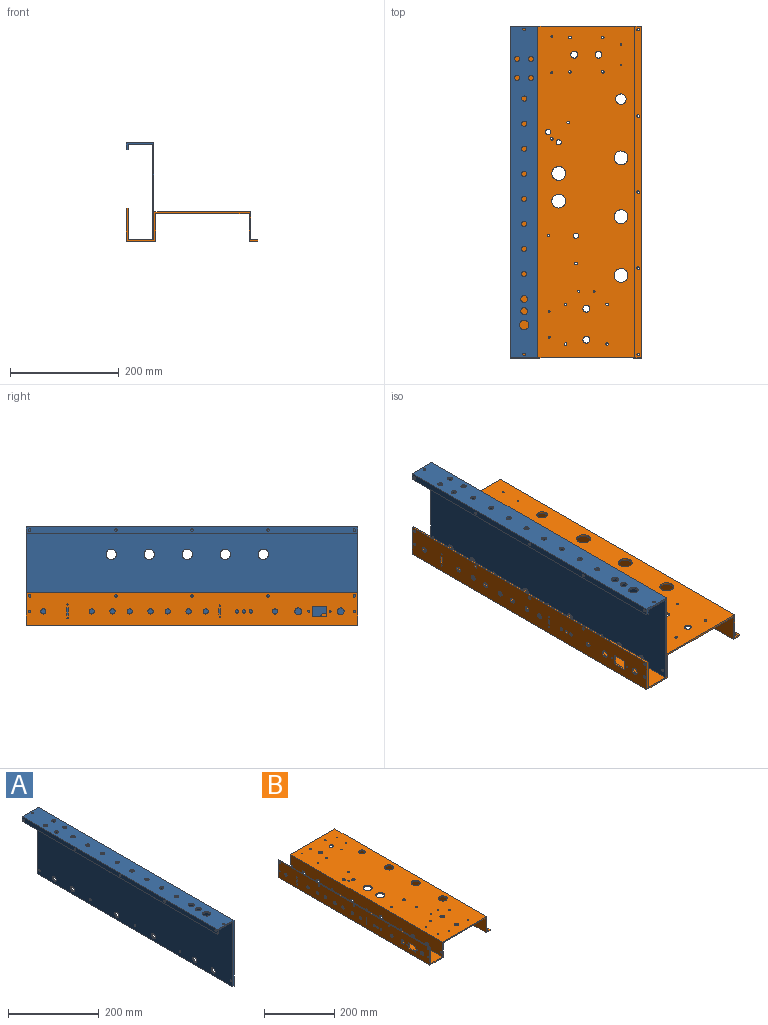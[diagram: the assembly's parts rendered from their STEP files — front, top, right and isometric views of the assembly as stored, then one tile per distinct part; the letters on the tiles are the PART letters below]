
ASSEMBLY  parts=2 mates=1
PART A: 48 faces, bbox 50.8x609.6x177.8 mm
  f0: plane 609.6x50.8mm, normal (0,0,1), area 29584.1mm2, adj f1,f7,f8,f9,f31,f32,f33,f34
  f1: plane 609.6x12.7mm, normal (-1,0,0), area 7652.9mm2, adj f0,f2,f8,f9,f26,f27,f28,f29
  f2: plane 609.6x3.18mm, normal (0,0,-1), area 1935.5mm2, adj f1,f3,f8,f9
  f3: plane 609.6x9.53mm, normal (1,0,0), area 5717.4mm2, adj f2,f4,f8,f9,f26,f27,f28,f29
  f4: plane 609.6x44.45mm, normal (0,0,-1), area 25713.2mm2, adj f3,f5,f8,f9,f31,f32,f33,f34
  f5: plane 609.6x174.63mm, normal (-1,0,0), area 104177.2mm2, adj f4,f6,f8,f9,f10,f11,f12,f13
  f6: plane 609.6x3.18mm, normal (0,0,-1), area 1935.5mm2, adj f5,f7,f8,f9
  f7: plane 609.6x177.8mm, normal (1,0,0), area 106112.6mm2, adj f0,f6,f8,f9,f10,f11,f12,f13
  f8: plane 177.8x50.8mm, normal (0,-1,0), area 746mm2, adj f0,f1,f2,f3,f4,f5,f6,f7
  f9: plane 177.8x50.8mm, normal (0,1,0), area 746mm2, adj f0,f1,f2,f3,f4,f5,f6,f7
  f10: cylinder r=9.53mm len=19.05mm, axis (1,0,0), area 190mm2, adj f5,f7
  f11: cylinder r=2.38mm len=4.76mm, axis (1,0,0), area 47.5mm2, adj f5,f7
  f12: cylinder r=6.35mm len=12.7mm, axis (1,0,0), area 126.7mm2, adj f5,f7
  f13: cylinder r=6.35mm len=12.7mm, axis (1,0,0), area 126.7mm2, adj f5,f7
  f14: cylinder r=2.38mm len=4.76mm, axis (1,0,0), area 47.5mm2, adj f5,f7
  f15: cylinder r=6.35mm len=12.7mm, axis (1,0,0), area 126.7mm2, adj f5,f7
  f16: cylinder r=2.38mm len=4.76mm, axis (1,0,0), area 47.5mm2, adj f5,f7
  f17: cylinder r=2.38mm len=4.76mm, axis (1,0,0), area 47.5mm2, adj f5,f7
  f18: cylinder r=6.35mm len=12.7mm, axis (1,0,0), area 126.7mm2, adj f5,f7
  f19: cylinder r=6.35mm len=12.7mm, axis (1,0,0), area 126.7mm2, adj f5,f7
  f20: cylinder r=6.35mm len=12.7mm, axis (1,0,0), area 126.7mm2, adj f5,f7
  f21: cylinder r=2.38mm len=4.76mm, axis (1,0,0), area 47.5mm2, adj f5,f7
  f22: cylinder r=9.53mm len=19.05mm, axis (1,0,0), area 190mm2, adj f5,f7
  f23: cylinder r=9.53mm len=19.05mm, axis (1,0,0), area 190mm2, adj f5,f7
  f24: cylinder r=9.53mm len=19.05mm, axis (1,0,0), area 190mm2, adj f5,f7
  f25: cylinder r=9.53mm len=19.05mm, axis (1,0,0), area 190mm2, adj f5,f7
  f26: cylinder r=2.38mm len=4.76mm, axis (-1,0,0), area 47.5mm2, adj f1,f3
  f27: cylinder r=2.38mm len=4.76mm, axis (-1,0,0), area 47.5mm2, adj f1,f3
  f28: cylinder r=2.38mm len=4.76mm, axis (-1,0,0), area 47.5mm2, adj f1,f3
  f29: cylinder r=2.38mm len=4.76mm, axis (-1,0,0), area 47.5mm2, adj f1,f3
  f30: cylinder r=2.38mm len=4.76mm, axis (-1,0,0), area 47.5mm2, adj f1,f3
  f31: cylinder r=4.76mm len=9.53mm, axis (0,0,1), area 95mm2, adj f0,f4
  f32: cylinder r=6.35mm len=12.7mm, axis (0,0,1), area 126.7mm2, adj f0,f4
  f33: cylinder r=4.76mm len=9.53mm, axis (0,0,1), area 95mm2, adj f0,f4
  f34: cylinder r=4.76mm len=9.53mm, axis (0,0,1), area 95mm2, adj f0,f4
  f35: cylinder r=6.35mm len=12.7mm, axis (0,0,1), area 126.7mm2, adj f0,f4
  f36: cylinder r=2.38mm len=4.76mm, axis (0,0,1), area 47.5mm2, adj f0,f4
  f37: cylinder r=2.38mm len=4.76mm, axis (0,0,1), area 47.5mm2, adj f0,f4
  f38: cylinder r=4.76mm len=9.53mm, axis (0,0,1), area 95mm2, adj f0,f4
  f39: cylinder r=8.73mm len=17.46mm, axis (0,0,1), area 174.2mm2, adj f0,f4
  f40: cylinder r=4.76mm len=9.53mm, axis (0,0,1), area 95mm2, adj f0,f4
  f41: cylinder r=4.76mm len=9.53mm, axis (0,0,1), area 95mm2, adj f0,f4
  f42: cylinder r=4.76mm len=9.53mm, axis (0,0,1), area 95mm2, adj f0,f4
  f43: cylinder r=4.76mm len=9.53mm, axis (0,0,1), area 95mm2, adj f0,f4
  f44: cylinder r=4.76mm len=9.53mm, axis (0,0,1), area 95mm2, adj f0,f4
  f45: cylinder r=4.76mm len=9.53mm, axis (0,0,1), area 95mm2, adj f0,f4
  f46: cylinder r=4.76mm len=9.53mm, axis (0,0,1), area 95mm2, adj f0,f4
  f47: cylinder r=4.76mm len=9.53mm, axis (0,0,1), area 95mm2, adj f0,f4
PART B: 104 faces, bbox 241.3x609.6x60.3 mm
  f0: plane 609.6x60.33mm, normal (-1,0,0), area 35038.9mm2, adj f2,f3,f14,f15,f16,f17,f18,f19
  f1: plane 609.6x57.15mm, normal (1,0,0), area 33103.4mm2, adj f2,f13,f14,f15,f16,f17,f18,f19
  f2: plane 609.6x3.18mm, normal (0,0,1), area 1935.5mm2, adj f0,f1,f14,f15
  f3: plane 609.6x53.98mm, normal (0,0,-1), area 32903.2mm2, adj f0,f4,f14,f15
  f4: plane 609.6x50.8mm, normal (1,0,0), area 30118.5mm2, adj f3,f5,f14,f15,f55,f56,f57,f58
  f5: plane 609.6x171.45mm, normal (0,0,-1), area 100699.8mm2, adj f4,f6,f14,f15,f66,f67,f68,f69
  f6: plane 609.6x50.8mm, normal (-1,0,0), area 30967.7mm2, adj f5,f7,f14,f15
  f7: plane 609.6x15.88mm, normal (0,0,-1), area 9588.3mm2, adj f6,f8,f14,f15,f99,f100,f101,f102
  f8: plane 609.6x3.18mm, normal (1,0,0), area 1935.5mm2, adj f7,f9,f14,f15
  f9: plane 609.6x12.7mm, normal (0,0,1), area 7652.9mm2, adj f8,f10,f14,f15,f99,f100,f101,f102
  f10: plane 609.6x50.8mm, normal (1,0,0), area 30967.7mm2, adj f9,f11,f14,f15
  f11: plane 609.6x177.8mm, normal (0,0,1), area 104570.7mm2, adj f10,f12,f14,f15,f66,f67,f68,f69
  f12: plane 609.6x50.8mm, normal (-1,0,0), area 30118.5mm2, adj f11,f13,f14,f15,f55,f56,f57,f58
  f13: plane 609.6x47.63mm, normal (0,0,1), area 29032.2mm2, adj f1,f12,f14,f15
  f14: plane 241.3x60.33mm, normal (0,-1,0), area 1270.2mm2, adj f0,f1,f2,f3,f4,f5,f6,f7
  f15: plane 241.3x60.33mm, normal (0,1,0), area 1270.2mm2, adj f0,f1,f2,f3,f4,f5,f6,f7
  f16: cylinder r=2.38mm len=4.76mm, axis (-1,0,0), area 47.5mm2, adj f0,f1
  f17: plane 9.53x3.18mm, normal (0,1,0), area 30.2mm2, adj f0,f1,f18,f20
  f18: plane 3.18x3.18mm, normal (0,0,-1), area 10.1mm2, adj f0,f1,f17,f19
  f19: plane 9.53x3.18mm, normal (0,-1,0), area 30.2mm2, adj f0,f1,f18,f20
  f20: plane 3.18x3.18mm, normal (0,0,1), area 10.1mm2, adj f0,f1,f17,f19
  f21: plane 13.49x3.18mm, normal (0,1,0), area 42.8mm2, adj f0,f1,f22,f24
  f22: plane 3.18x3.18mm, normal (0,0,-1), area 10.1mm2, adj f0,f1,f21,f23
  f23: plane 13.49x3.18mm, normal (0,-1,0), area 42.8mm2, adj f0,f1,f22,f24
  f24: plane 3.18x3.18mm, normal (0,0,1), area 10.1mm2, adj f0,f1,f21,f23
  f25: cylinder r=2.38mm len=4.76mm, axis (-1,0,0), area 47.5mm2, adj f0,f1
  f26: cylinder r=6.35mm len=12.7mm, axis (-1,0,0), area 126.7mm2, adj f0,f1
  f27: cylinder r=1.59mm len=3.18mm, axis (-1,0,0), area 31.7mm2, adj f0,f1
  f28: cylinder r=3.17mm len=6.35mm, axis (-1,0,0), area 63.3mm2, adj f0,f1
  f29: cylinder r=4.76mm len=9.53mm, axis (-1,0,0), area 95mm2, adj f0,f1
  f30: cylinder r=1.59mm len=3.18mm, axis (-1,0,0), area 31.7mm2, adj f0,f1
  f31: cylinder r=1.19mm len=3.18mm, axis (-1,0,0), area 23.8mm2, adj f0,f1
  f32: plane 19.05x3.18mm, normal (0,1,0), area 60.5mm2, adj f0,f1,f33,f35
  f33: plane 26.99x3.18mm, normal (0,0,-1), area 85.7mm2, adj f0,f1,f32,f34
  f34: plane 19.05x3.18mm, normal (0,-1,0), area 60.5mm2, adj f0,f1,f33,f35
  f35: plane 26.99x3.18mm, normal (0,0,1), area 85.7mm2, adj f0,f1,f32,f34
  f36: cylinder r=1.19mm len=3.18mm, axis (-1,0,0), area 23.8mm2, adj f0,f1
  f37: cylinder r=1.19mm len=3.18mm, axis (-1,0,0), area 23.8mm2, adj f0,f1
  f38: cylinder r=1.19mm len=3.18mm, axis (-1,0,0), area 23.8mm2, adj f0,f1
  f39: cylinder r=2.38mm len=4.76mm, axis (-1,0,0), area 47.5mm2, adj f0,f1
  f40: cylinder r=2.38mm len=4.76mm, axis (-1,0,0), area 47.5mm2, adj f0,f1
  f41: cylinder r=2.38mm len=4.76mm, axis (-1,0,0), area 47.5mm2, adj f0,f1
  f42: cylinder r=2.38mm len=4.76mm, axis (-1,0,0), area 47.5mm2, adj f0,f1
  f43: cylinder r=2.38mm len=4.76mm, axis (-1,0,0), area 47.5mm2, adj f0,f1
  f44: cylinder r=4.76mm len=9.53mm, axis (-1,0,0), area 95mm2, adj f0,f1
  f45: cylinder r=4.76mm len=9.53mm, axis (-1,0,0), area 95mm2, adj f0,f1
  f46: cylinder r=4.76mm len=9.53mm, axis (-1,0,0), area 95mm2, adj f0,f1
  f47: cylinder r=4.76mm len=9.53mm, axis (-1,0,0), area 95mm2, adj f0,f1
  f48: cylinder r=4.76mm len=9.53mm, axis (-1,0,0), area 95mm2, adj f0,f1
  f49: cylinder r=4.76mm len=9.53mm, axis (-1,0,0), area 95mm2, adj f0,f1
  f50: cylinder r=4.76mm len=9.53mm, axis (-1,0,0), area 95mm2, adj f0,f1
  f51: cylinder r=4.76mm len=9.53mm, axis (-1,0,0), area 95mm2, adj f0,f1
  f52: cylinder r=3.17mm len=6.35mm, axis (-1,0,0), area 63.3mm2, adj f0,f1
  f53: cylinder r=3.17mm len=6.35mm, axis (-1,0,0), area 63.3mm2, adj f0,f1
  f54: cylinder r=6.35mm len=12.7mm, axis (-1,0,0), area 126.7mm2, adj f0,f1
  f55: cylinder r=2.38mm len=4.76mm, axis (1,0,0), area 47.5mm2, adj f4,f12
  f56: cylinder r=6.35mm len=12.7mm, axis (1,0,0), area 126.7mm2, adj f4,f12
  f57: cylinder r=6.35mm len=12.7mm, axis (1,0,0), area 126.7mm2, adj f4,f12
  f58: cylinder r=2.38mm len=4.76mm, axis (1,0,0), area 47.5mm2, adj f4,f12
  f59: cylinder r=6.35mm len=12.7mm, axis (1,0,0), area 126.7mm2, adj f4,f12
  f60: cylinder r=2.38mm len=4.76mm, axis (1,0,0), area 47.5mm2, adj f4,f12
  f61: cylinder r=6.35mm len=12.7mm, axis (1,0,0), area 126.7mm2, adj f4,f12
  f62: cylinder r=2.38mm len=4.76mm, axis (1,0,0), area 47.5mm2, adj f4,f12
  f63: cylinder r=6.35mm len=12.7mm, axis (1,0,0), area 126.7mm2, adj f4,f12
  f64: cylinder r=6.35mm len=12.7mm, axis (1,0,0), area 126.7mm2, adj f4,f12
  f65: cylinder r=2.38mm len=4.76mm, axis (1,0,0), area 47.5mm2, adj f4,f12
  f66: cylinder r=1.59mm len=3.18mm, axis (0,0,1), area 31.7mm2, adj f5,f11
  f67: cylinder r=1.59mm len=3.18mm, axis (0,0,1), area 31.7mm2, adj f5,f11
  f68: cylinder r=6.35mm len=12.7mm, axis (0,0,1), area 126.7mm2, adj f5,f11
  f69: cylinder r=2.38mm len=4.76mm, axis (0,0,1), area 47.5mm2, adj f5,f11
  f70: cylinder r=4.76mm len=9.53mm, axis (0,0,1), area 95mm2, adj f5,f11
  f71: cylinder r=1.59mm len=3.18mm, axis (0,0,1), area 31.7mm2, adj f5,f11
  f72: cylinder r=2.38mm len=4.76mm, axis (0,0,1), area 47.5mm2, adj f5,f11
  f73: cylinder r=2.38mm len=4.76mm, axis (0,0,1), area 47.5mm2, adj f5,f11
  f74: cylinder r=2.38mm len=4.76mm, axis (0,0,1), area 47.5mm2, adj f5,f11
  f75: cylinder r=2.38mm len=4.76mm, axis (0,0,1), area 47.5mm2, adj f5,f11
  f76: cylinder r=2.38mm len=4.76mm, axis (0,0,1), area 47.5mm2, adj f5,f11
  f77: cylinder r=6.35mm len=12.7mm, axis (0,0,1), area 126.7mm2, adj f5,f11
  f78: cylinder r=1.59mm len=3.18mm, axis (0,0,1), area 31.7mm2, adj f5,f11
  f79: cylinder r=9.53mm len=19.05mm, axis (0,0,1), area 190mm2, adj f5,f11
  f80: cylinder r=12.7mm len=25.4mm, axis (0,0,1), area 253.4mm2, adj f5,f11
  f81: cylinder r=12.7mm len=25.4mm, axis (0,0,1), area 253.4mm2, adj f5,f11
  f82: cylinder r=12.7mm len=25.4mm, axis (0,0,1), area 253.4mm2, adj f5,f11
  f83: cylinder r=6.35mm len=12.7mm, axis (0,0,1), area 126.7mm2, adj f5,f11
  f84: cylinder r=2.38mm len=4.76mm, axis (0,0,1), area 47.5mm2, adj f5,f11
  f85: cylinder r=2.38mm len=4.76mm, axis (0,0,1), area 47.5mm2, adj f5,f11
  f86: cylinder r=1.59mm len=3.18mm, axis (0,0,1), area 31.7mm2, adj f5,f11
  f87: cylinder r=1.59mm len=3.18mm, axis (0,0,1), area 31.7mm2, adj f5,f11
  f88: cylinder r=2.38mm len=4.76mm, axis (0,0,1), area 47.5mm2, adj f5,f11
  f89: cylinder r=2.38mm len=4.76mm, axis (0,0,1), area 47.5mm2, adj f5,f11
  f90: cylinder r=6.35mm len=12.7mm, axis (0,0,1), area 126.7mm2, adj f5,f11
  f91: cylinder r=1.59mm len=3.18mm, axis (0,0,1), area 31.7mm2, adj f5,f11
  f92: cylinder r=12.7mm len=25.4mm, axis (0,0,1), area 253.4mm2, adj f5,f11
  f93: cylinder r=12.7mm len=25.4mm, axis (0,0,1), area 253.4mm2, adj f5,f11
  f94: cylinder r=4.76mm len=9.53mm, axis (0,0,1), area 95mm2, adj f5,f11
  f95: cylinder r=2.38mm len=4.76mm, axis (0,0,1), area 47.5mm2, adj f5,f11
  f96: cylinder r=4.76mm len=9.53mm, axis (0,0,1), area 95mm2, adj f5,f11
  f97: cylinder r=2.38mm len=4.76mm, axis (0,0,1), area 47.5mm2, adj f5,f11
  f98: cylinder r=1.59mm len=3.18mm, axis (0,0,1), area 31.7mm2, adj f5,f11
  f99: cylinder r=2.38mm len=4.76mm, axis (0,0,1), area 47.5mm2, adj f7,f9
  f100: cylinder r=2.38mm len=4.76mm, axis (0,0,1), area 47.5mm2, adj f7,f9
  f101: cylinder r=2.38mm len=4.76mm, axis (0,0,1), area 47.5mm2, adj f7,f9
  f102: cylinder r=2.38mm len=4.76mm, axis (0,0,1), area 47.5mm2, adj f7,f9
  f103: cylinder r=2.38mm len=4.76mm, axis (0,0,1), area 47.5mm2, adj f7,f9
PLACE A t=(-204.93,141.24,-87.85)mm
PLACE B t=(-119.87,141.24,-152.66)mm
MATE fastened A.f21 <-> B.f55  axis (1,0,0) through (-182.06,-462.01,-161.08)mm
